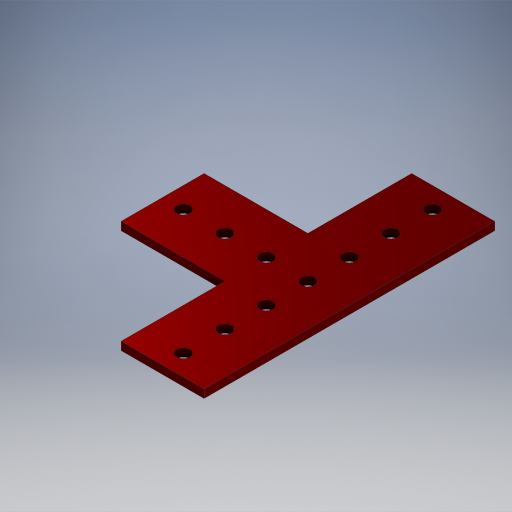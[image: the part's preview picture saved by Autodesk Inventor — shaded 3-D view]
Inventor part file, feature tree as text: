
AUTODESK INVENTOR PART (.ipt)
format: ipt  version: 2024.2 (Build 282272000, 272)  size: 350,208 bytes
history: native  units: in
note: dims shown in document units (in); Inventor stores cm internally (conversion verified against a paired STEP export)
features: extrude x2, sketch x2, projected_geometry x2
ambient origin geometry x8: Origin, YZ Plane, XZ Plane, XY Plane, X Axis, Y Axis, Z Axis, Center Point
bodies: Solid2 (feature_tree), Solid1 (feature_tree)
feature tree (6):
  extrude  "Extrusion1"  Depth=0.375in TaperAngle=0.0deg
  extrude  "Extrusion2"  Depth=1.0in TaperAngle=0.0deg
  sketch  "Sketch1"  dims[d0=0.5in d1=0.375in d2=0.0in]
  projected_geometry  "Projected Loop1"
  sketch  "Sketch2"  dims[d3=1.0in d4=0.1875in d5=0.0in]
  projected_geometry  "Projected Loop2"
